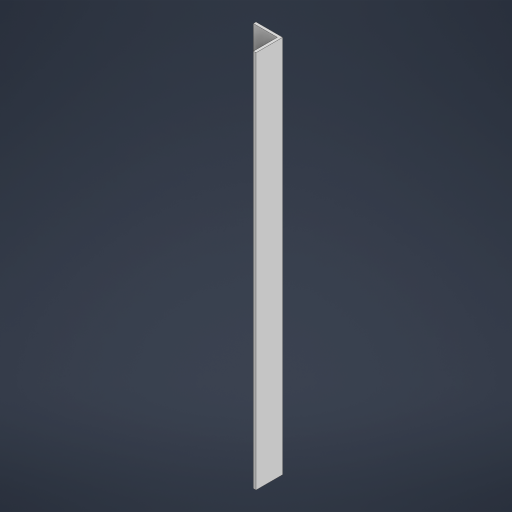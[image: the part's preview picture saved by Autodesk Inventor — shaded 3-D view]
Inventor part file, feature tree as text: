
AUTODESK INVENTOR PART (.ipt)
format: ipt  version: 2024 (Build 280153000, 153)  size: 235,520 bytes
history: native  units: mm
features: extrude x1, sketch x1
ambient origin geometry x8: Origin, YZ Plane, XZ Plane, XY Plane, X Axis, Y Axis, Z Axis, Center Point
bodies: Solid1 (feature_tree)
feature tree (2):
  extrude  "Extrusion1"  Depth=50.0mm
  sketch  "Sketch1"  dims[d0=50.0mm d1=50.0mm d3=5.0mm d4=5.0mm d5=711.0mm d6=0.0mm]
